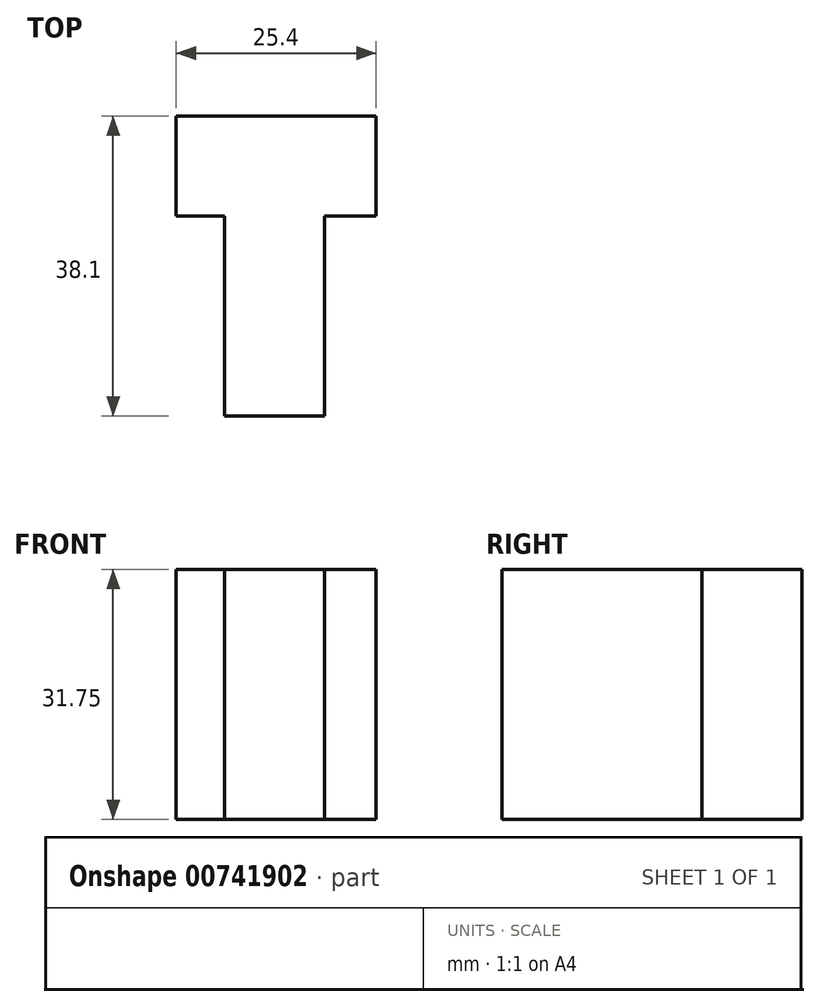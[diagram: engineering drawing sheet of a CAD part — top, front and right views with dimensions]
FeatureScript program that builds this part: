
annotation { "Feature Type Name" : "Feature", "Feature Type Description" : "" }
export const myFeature = defineFeature(function(context is Context, id is Id, definition is map)
    precondition{}
    {
        {
            var Q0;
            Q0=qCreatedBy(makeId("Top.planeOp"),FACE);
            var sketch = newSketch(context, id + "F0", { "sketchPlane" : qUnion([Q0])});
            skLineSegment(sketch, "E0", {"start": v(0, 0) * mm, "end": v(0, 25.4) * mm});
            skLineSegment(sketch, "E1", {"start": v(0, 25.4) * mm, "end": v(-6.17, 25.4) * mm});
            skLineSegment(sketch, "E2", {"start": v(-6.17, 25.4) * mm, "end": v(-6.17, 38.1) * mm});
            skLineSegment(sketch, "E3", {"start": v(-6.17, 38.1) * mm, "end": v(19.23, 38.1) * mm});
            skLineSegment(sketch, "E4", {"start": v(19.23, 38.1) * mm, "end": v(19.23, 25.4) * mm});
            skLineSegment(sketch, "E5", {"start": v(19.23, 25.4) * mm, "end": v(12.7, 25.4) * mm});
            skLineSegment(sketch, "E6", {"start": v(12.7, 25.4) * mm, "end": v(12.7, 0) * mm});
            skLineSegment(sketch, "E7", {"start": v(12.7, 0) * mm, "end": v(0, 0) * mm});
            skSolve(sketch);
        }
        {
            var Q0;
            Q0 = qSketchRegion(id + "F0", true);
            extrude(context, id + "F1", {"entities" : qUnion([Q0]), "depth" : 31.75 * mm, "offsetDistance" : 25.4 * mm});
        }
    });
